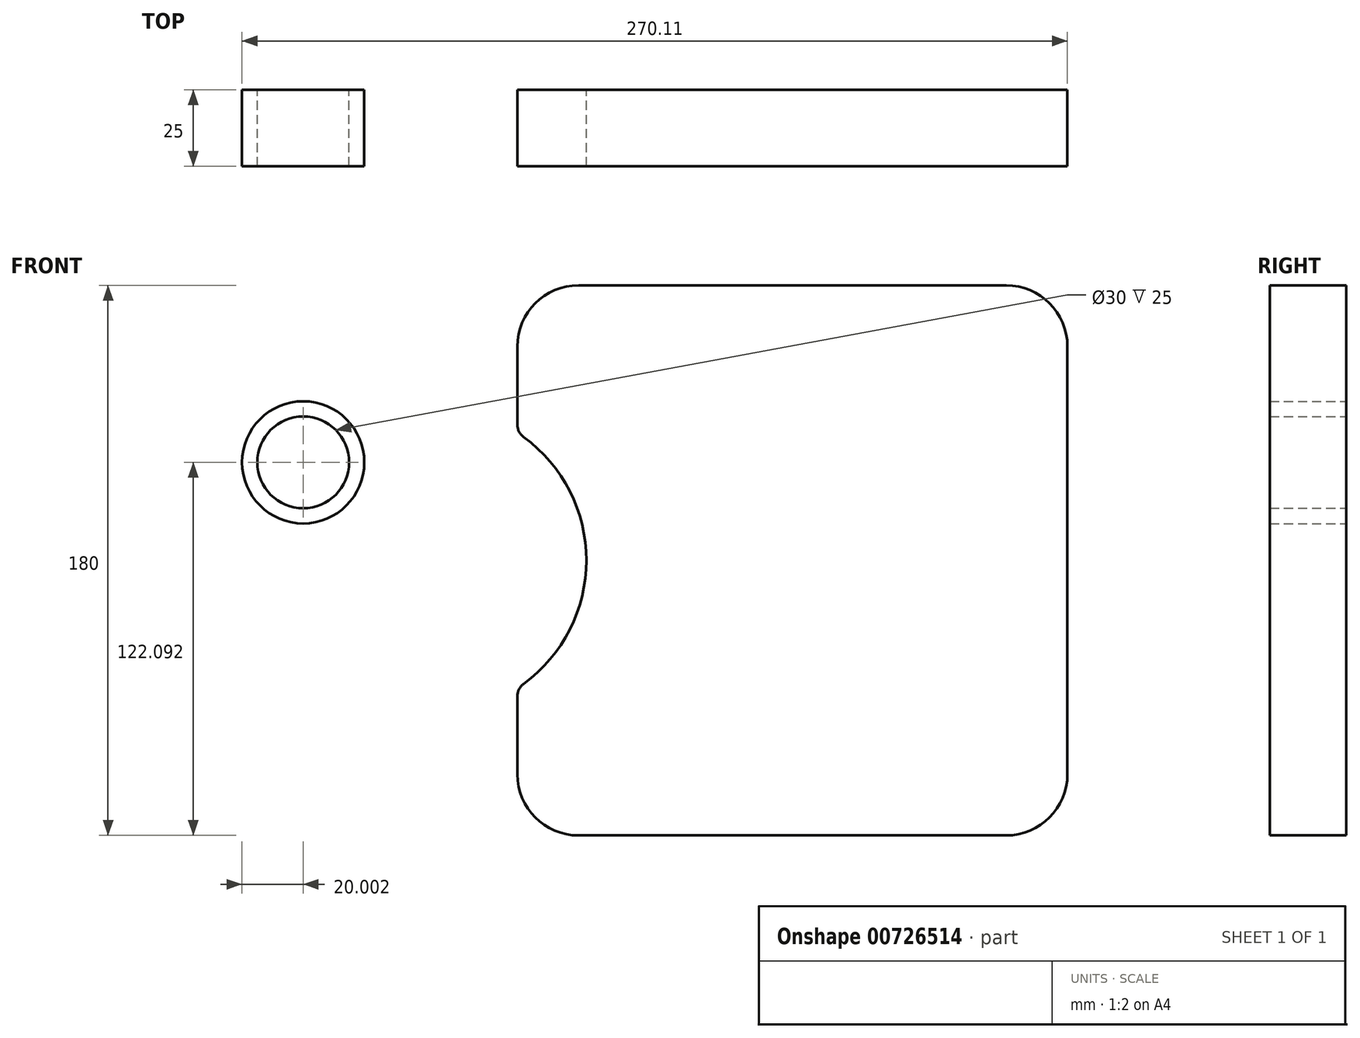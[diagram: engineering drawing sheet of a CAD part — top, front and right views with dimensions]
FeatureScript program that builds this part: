
annotation { "Feature Type Name" : "Feature", "Feature Type Description" : "" }
export const myFeature = defineFeature(function(context is Context, id is Id, definition is map)
    precondition{}
    {
        {
            var Q0;
            Q0=qCreatedBy(makeId("Front.planeOp"),FACE);
            var sketch = newSketch(context, id + "F0", { "sketchPlane" : qUnion([Q0])});
            skLineSegment(sketch, "E0.bottom", {"start": v(-70, 90) * mm, "end": v(70, 90) * mm});
            skLineSegment(sketch, "E0.top", {"start": v(-70, -90) * mm, "end": v(70, -90) * mm});
            skLineSegment(sketch, "E0.left", {"start": v(-90, 70) * mm, "end": v(-90, -70) * mm});
            skLineSegment(sketch, "E0.right", {"start": v(90, 70) * mm, "end": v(90, -70) * mm});
            skPoint(sketch, "E0.middle", {"position": v(0, 0) * mm});
            skPoint(sketch, "E1.visualSharp", {"position": v(-90, 90) * mm});
            skArc(sketch, "E1.filletArc", {"start": v(-70, 90) * mm, "mid": v(-84.14, 84.14) * mm, "end": v(-90, 70) * mm});
            skPoint(sketch, "E2.visualSharp", {"position": v(90, 90) * mm});
            skArc(sketch, "E2.filletArc", {"start": v(90, 70) * mm, "mid": v(84.14, 84.14) * mm, "end": v(70, 90) * mm});
            skPoint(sketch, "E3.visualSharp", {"position": v(90, -90) * mm});
            skArc(sketch, "E3.filletArc", {"start": v(70, -90) * mm, "mid": v(84.14, -84.14) * mm, "end": v(90, -70) * mm});
            skPoint(sketch, "E4.visualSharp", {"position": v(-90, -90) * mm});
            skArc(sketch, "E4.filletArc", {"start": v(-90, -70) * mm, "mid": v(-84.14, -84.14) * mm, "end": v(-70, -90) * mm});
            skArc(sketch, "E5", {"start": v(-90, -41.8) * mm, "mid": v(-67.45, 0) * mm, "end": v(-90, 41.8) * mm});
            skSolve(sketch);
        }
        {
            var Q0;
            Q0=makeQuery(id+"F0.imprint","IMPRINT",FACE,{"disambiguationData":[TD([[makeQuery(id+"F0.imprint","IMPRINT",EDGE,{"derivedFrom":sQuery(id+"F0.wireOp",EDGE,"E0.bottom")}),-1.0]])]});
            extrude(context, id + "F1", {"entities" : qUnion([Q0]), "depth" : 25 * mm, "offsetDistance" : 25 * mm});
        }
        {
            var Q0;
            Q0=qCreatedBy(makeId("Front.planeOp"),FACE);
            var sketch = newSketch(context, id + "F2", { "sketchPlane" : qUnion([Q0])});
            skCircle(sketch, "E6", {"center": v(-160.1, 32.1) * mm, "radius": 20 * mm});
            skCircle(sketch, "E7", {"center": v(-160.1, 32.1) * mm, "radius": 15 * mm});
            skSolve(sketch);
        }
        {
            var Q0;
            Q0=makeQuery(id+"F2.imprint","IMPRINT",FACE,{"disambiguationData":[TD([[makeQuery(id+"F2.imprint","IMPRINT",EDGE,{"derivedFrom":sQuery(id+"F2.wireOp",EDGE,"E6")}),1.0]])]});
            extrude(context, id + "F3", {"entities" : qUnion([Q0]), "depth" : 25 * mm, "offsetDistance" : 25 * mm});
        }
        {
            var Q0;
            {var subQ0=sQuery(id+"F0.wireOp",EDGE,"E5");var subQ1=sQuery(id+"F0.wireOp",EDGE,"E0.left");Q0=makeQuery(id+"F1.opExtrude","SWEPT_EDGE",EDGE,{"disambiguationData":[OSD([subQ1,subQ0]),TDD([makeQuery(id+"F0.imprint","INTERSECT",VERTEX,{"disambiguationData":[OD(1.0)],"derivedFrom":[subQ1,subQ0]})])]});}
            var Q1;
            {var subQ0=sQuery(id+"F0.wireOp",EDGE,"E5");var subQ1=sQuery(id+"F0.wireOp",EDGE,"E0.left");Q1=makeQuery(id+"F1.opExtrude","SWEPT_EDGE",EDGE,{"disambiguationData":[OSD([subQ1,subQ0]),TDD([makeQuery(id+"F0.imprint","INTERSECT",VERTEX,{"disambiguationData":[OD(0.0)],"derivedFrom":[subQ1,subQ0]})])]});}
            fillet(context, id + "F4", {"entities" : qUnion([Q0, Q1]), "radius" : 5 * mm, "tangentPropagation" : true, "allowEdgeOverflow" : false});
        }
    });
